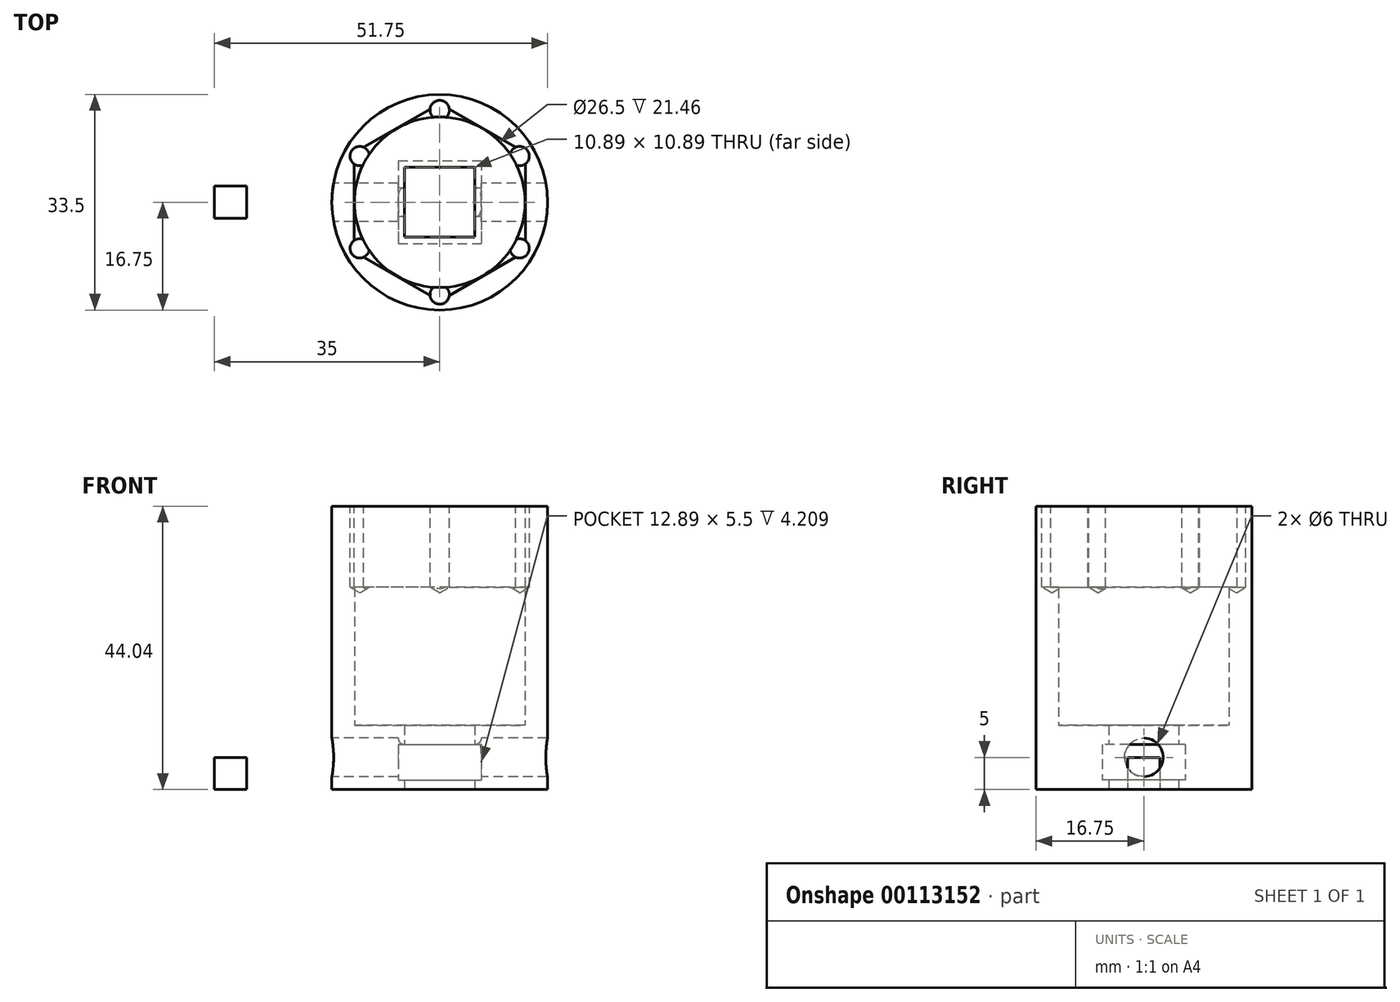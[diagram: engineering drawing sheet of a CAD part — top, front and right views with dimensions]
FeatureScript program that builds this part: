
annotation { "Feature Type Name" : "Feature", "Feature Type Description" : "" }
export const myFeature = defineFeature(function(context is Context, id is Id, definition is map)
    precondition{}
    {
        {
            var Q0;
            Q0=qCreatedBy(makeId("Top.planeOp"),FACE);
            var sketch = newSketch(context, id + "F0", { "sketchPlane" : qUnion([Q0])});
            skCircle(sketch, "E0", {"center": v(0, 0) * mm, "radius": 16.75 * mm});
            skLineSegment(sketch, "E1", {"start": v(0, 0) * mm, "end": v(0, 15.35) * mm});
            skLineSegment(sketch, "E2", {"start": v(0, 15.35) * mm, "end": v(-13.29, 7.67) * mm});
            skLineSegment(sketch, "E3", {"start": v(-13.3, 7.67) * mm, "end": v(-13.3, -7.67) * mm});
            skLineSegment(sketch, "E4", {"start": v(-13.3, -7.67) * mm, "end": v(0, -15.35) * mm});
            skLineSegment(sketch, "E5", {"start": v(0, -15.35) * mm, "end": v(13.29, -7.67) * mm});
            skLineSegment(sketch, "E6", {"start": v(13.29, -7.67) * mm, "end": v(13.29, 7.67) * mm});
            skLineSegment(sketch, "E7", {"start": v(0, 0) * mm, "end": v(0, -15.35) * mm});
            skLineSegment(sketch, "E8", {"start": v(0, 15.35) * mm, "end": v(13.3, 7.67) * mm});
            skLineSegment(sketch, "E9", {"start": v(0, 0) * mm, "end": v(13.29, 7.67) * mm});
            skLineSegment(sketch, "E10", {"start": v(0, 0) * mm, "end": v(13.29, -7.67) * mm});
            skLineSegment(sketch, "E11", {"start": v(0, 0) * mm, "end": v(-13.29, -7.67) * mm});
            skLineSegment(sketch, "E12", {"start": v(0, 0) * mm, "end": v(-13.3, 7.67) * mm});
            skCircle(sketch, "E13", {"center": v(0, 0) * mm, "radius": 15.75 * mm});
            skCircle(sketch, "E14", {"center": v(0, 0) * mm, "radius": 13.25 * mm});
            skLineSegment(sketch, "E15.bottom", {"start": v(-35, 2.5) * mm, "end": v(-30, 2.5) * mm});
            skLineSegment(sketch, "E15.top", {"start": v(-35, -2.5) * mm, "end": v(-30, -2.5) * mm});
            skLineSegment(sketch, "E15.left", {"start": v(-35, 2.5) * mm, "end": v(-35, -2.5) * mm});
            skLineSegment(sketch, "E15.right", {"start": v(-30, 2.5) * mm, "end": v(-30, -2.5) * mm});
            skPoint(sketch, "E15.middle", {"position": v(-32.5, 0) * mm});
            skLineSegment(sketch, "E16", {"start": v(-32.5, 0) * mm, "end": v(-35, 0) * mm});
            skLineSegment(sketch, "E17", {"start": v(-32.5, 0) * mm, "end": v(-30, 0) * mm});
            skLineSegment(sketch, "E18.bottom", {"start": v(-5.44, 5.45) * mm, "end": v(5.45, 5.45) * mm});
            skLineSegment(sketch, "E18.top", {"start": v(-5.45, -5.44) * mm, "end": v(5.44, -5.44) * mm});
            skLineSegment(sketch, "E18.left", {"start": v(-5.44, 5.45) * mm, "end": v(-5.45, -5.45) * mm});
            skLineSegment(sketch, "E18.right", {"start": v(5.45, 5.45) * mm, "end": v(5.44, -5.45) * mm});
            skLineSegment(sketch, "E19.bottom", {"start": v(-6.44, 6.45) * mm, "end": v(6.45, 6.45) * mm});
            skLineSegment(sketch, "E19.top", {"start": v(-6.45, -6.44) * mm, "end": v(6.44, -6.44) * mm});
            skLineSegment(sketch, "E19.left", {"start": v(-6.44, 6.45) * mm, "end": v(-6.45, -6.44) * mm});
            skLineSegment(sketch, "E19.right", {"start": v(6.45, 6.45) * mm, "end": v(6.44, -6.44) * mm});
            skSolve(sketch);
        }
        {
            var Q0;
            {var subQ0=sQuery(id+"F0.wireOp",EDGE,"E3");Q0=makeQuery(id+"F0.imprint","IMPRINT",FACE,{"disambiguationData":[TD([[makeQuery(id+"F0.imprint","IMPRINT",EDGE,{"derivedFrom":subQ0}),1.0]])]});}
            var Q1;
            {var subQ0=sQuery(id+"F0.wireOp",EDGE,"E4");Q1=makeQuery(id+"F0.imprint","IMPRINT",FACE,{"disambiguationData":[TD([[makeQuery(id+"F0.imprint","IMPRINT",EDGE,{"derivedFrom":subQ0}),1.0]])]});}
            var Q2;
            {var subQ0=sQuery(id+"F0.wireOp",EDGE,"E5");Q2=makeQuery(id+"F0.imprint","IMPRINT",FACE,{"disambiguationData":[TD([[makeQuery(id+"F0.imprint","IMPRINT",EDGE,{"derivedFrom":subQ0}),1.0]])]});}
            var Q3;
            {var subQ0=sQuery(id+"F0.wireOp",EDGE,"E8");Q3=makeQuery(id+"F0.imprint","IMPRINT",FACE,{"disambiguationData":[TD([[makeQuery(id+"F0.imprint","IMPRINT",EDGE,{"derivedFrom":subQ0}),-1.0]])]});}
            var Q4;
            {var subQ0=sQuery(id+"F0.wireOp",EDGE,"E2");Q4=makeQuery(id+"F0.imprint","IMPRINT",FACE,{"disambiguationData":[TD([[makeQuery(id+"F0.imprint","IMPRINT",EDGE,{"derivedFrom":subQ0}),1.0]])]});}
            var Q5;
            {var subQ0=sQuery(id+"F0.wireOp",EDGE,"E2");Q5=makeQuery(id+"F0.imprint","IMPRINT",FACE,{"disambiguationData":[TD([[makeQuery(id+"F0.imprint","IMPRINT",EDGE,{"derivedFrom":subQ0}),1.0]])]});}
            var Q6;
            {var subQ0=sQuery(id+"F0.wireOp",EDGE,"E6");Q6=makeQuery(id+"F0.imprint","IMPRINT",FACE,{"disambiguationData":[TD([[makeQuery(id+"F0.imprint","IMPRINT",EDGE,{"derivedFrom":subQ0}),1.0]])]});}
            extrude(context, id + "F1", {"entities" : qUnion([Q0, Q1, Q2, Q3, Q4, Q5, Q6]), "depth" : 31.46 * mm});
        }
        {
            var Q0;
            Q0=makeQuery(id+"F0.imprint","IMPRINT",FACE,{"disambiguationData":[TD([[makeQuery(id+"F0.imprint","IMPRINT",EDGE,{"derivedFrom":sQuery(id+"F0.wireOp",EDGE,"E0")}),1.0]])]});
            var Q1;
            Q1=makeQuery(id+"F0.imprint","IMPRINT",FACE,{"disambiguationData":[TD([[makeQuery(id+"F0.imprint","IMPRINT",EDGE,{"derivedFrom":sQuery(id+"F0.wireOp",EDGE,"E2")}),-1.0]])]});
            extrude(context, id + "F2", {"entities" : qUnion([Q0, Q1]), "operationType" : NewBodyOperationType.ADD, "depth" : 44.04 * mm});
        }
        {
            var Q0;
            {var subQ1=sQuery(id+"F0.wireOp",EDGE,"E11");var subQ3=sQuery(id+"F0.wireOp",EDGE,"E14");var subQ4=makeQuery(id+"F0.imprint","INTERSECT",VERTEX,{"derivedFrom":[subQ1,subQ3]});Q0=makeQuery(id+"F0.imprint","IMPRINT",FACE,{"disambiguationData":[TD([[makeQuery(id+"F0.imprint","IMPRINT",EDGE,{"disambiguationData":[TD([[subQ4,1.0]])],"derivedFrom":subQ3}),1.0]])]});}
            var Q1;
            {var subQ1=sQuery(id+"F0.wireOp",EDGE,"E1");var subQ3=sQuery(id+"F0.wireOp",EDGE,"E14");var subQ4=makeQuery(id+"F0.imprint","INTERSECT",VERTEX,{"derivedFrom":[subQ1,subQ3]});Q1=makeQuery(id+"F0.imprint","IMPRINT",FACE,{"disambiguationData":[TD([[makeQuery(id+"F0.imprint","IMPRINT",EDGE,{"disambiguationData":[TD([[subQ4,-1.0]])],"derivedFrom":subQ3}),1.0]])]});}
            var Q2;
            {var subQ1=sQuery(id+"F0.wireOp",EDGE,"E1");var subQ3=sQuery(id+"F0.wireOp",EDGE,"E14");var subQ4=makeQuery(id+"F0.imprint","INTERSECT",VERTEX,{"derivedFrom":[subQ1,subQ3]});Q2=makeQuery(id+"F0.imprint","IMPRINT",FACE,{"disambiguationData":[TD([[makeQuery(id+"F0.imprint","IMPRINT",EDGE,{"disambiguationData":[TD([[subQ4,1.0]])],"derivedFrom":subQ3}),1.0]])]});}
            var Q3;
            {var subQ1=sQuery(id+"F0.wireOp",EDGE,"E9");var subQ3=sQuery(id+"F0.wireOp",EDGE,"E14");var subQ4=makeQuery(id+"F0.imprint","INTERSECT",VERTEX,{"derivedFrom":[subQ1,subQ3]});Q3=makeQuery(id+"F0.imprint","IMPRINT",FACE,{"disambiguationData":[TD([[makeQuery(id+"F0.imprint","IMPRINT",EDGE,{"disambiguationData":[TD([[subQ4,1.0]])],"derivedFrom":subQ3}),1.0]])]});}
            var Q4;
            {var subQ1=sQuery(id+"F0.wireOp",EDGE,"E7");var subQ3=sQuery(id+"F0.wireOp",EDGE,"E14");var subQ4=makeQuery(id+"F0.imprint","INTERSECT",VERTEX,{"derivedFrom":[subQ1,subQ3]});Q4=makeQuery(id+"F0.imprint","IMPRINT",FACE,{"disambiguationData":[TD([[makeQuery(id+"F0.imprint","IMPRINT",EDGE,{"disambiguationData":[TD([[subQ4,-1.0]])],"derivedFrom":subQ3}),1.0]])]});}
            var Q5;
            {var subQ1=sQuery(id+"F0.wireOp",EDGE,"E7");var subQ3=sQuery(id+"F0.wireOp",EDGE,"E14");var subQ4=makeQuery(id+"F0.imprint","INTERSECT",VERTEX,{"derivedFrom":[subQ1,subQ3]});Q5=makeQuery(id+"F0.imprint","IMPRINT",FACE,{"disambiguationData":[TD([[makeQuery(id+"F0.imprint","IMPRINT",EDGE,{"disambiguationData":[TD([[subQ4,1.0]])],"derivedFrom":subQ3}),1.0]])]});}
            extrude(context, id + "F3", {"entities" : qUnion([Q0, Q1, Q2, Q3, Q4, Q5]), "operationType" : NewBodyOperationType.ADD, "depth" : 10 * mm});
        }
        {
            var Q0;
            Q0=makeQuery(id+"F2.opExtrude","CAP_FACE",FACE,{"disambiguationData":[OSD([sQuery(id+"F0.wireOp",EDGE,"E0"),sQuery(id+"F0.wireOp",EDGE,"E2"),sQuery(id+"F0.wireOp",EDGE,"E3"),sQuery(id+"F0.wireOp",EDGE,"E4"),sQuery(id+"F0.wireOp",EDGE,"E5"),sQuery(id+"F0.wireOp",EDGE,"E6"),sQuery(id+"F0.wireOp",EDGE,"E8")])],"isStart":false});
            var sketch = newSketch(context, id + "F4", { "sketchPlane" : qUnion([Q0])});
            skLineSegment(sketch, "E20", {"start": v(0, 15.35) * mm, "end": v(-13.29, 7.67) * mm});
            skLineSegment(sketch, "E21", {"start": v(-13.3, 7.67) * mm, "end": v(-13.29, -7.67) * mm});
            skLineSegment(sketch, "E22", {"start": v(-13.29, -7.67) * mm, "end": v(0, -15.35) * mm});
            skLineSegment(sketch, "E23", {"start": v(0, -15.35) * mm, "end": v(13.29, -7.67) * mm});
            skLineSegment(sketch, "E24", {"start": v(13.29, -7.67) * mm, "end": v(13.29, 7.67) * mm});
            skLineSegment(sketch, "E25", {"start": v(13.29, 7.67) * mm, "end": v(0, 15.35) * mm});
            skLineSegment(sketch, "E26", {"start": v(0, 15.35) * mm, "end": v(0, 14.35) * mm});
            skLineSegment(sketch, "E27", {"start": v(13.29, 7.67) * mm, "end": v(12.42, 7.17) * mm});
            skLineSegment(sketch, "E28", {"start": v(-13.29, 7.67) * mm, "end": v(-12.42, 7.17) * mm});
            skLineSegment(sketch, "E29", {"start": v(-13.3, -7.67) * mm, "end": v(-12.42, -7.17) * mm});
            skLineSegment(sketch, "E30", {"start": v(13.29, -7.67) * mm, "end": v(12.42, -7.17) * mm});
            skLineSegment(sketch, "E31", {"start": v(0, -15.35) * mm, "end": v(0, -14.35) * mm});
            skSolve(sketch);
        }
        {
            var Q0;
            Q0=sQuery(id+"F4.wireOp",VERTEX,"E28.end");
            var Q1;
            Q1=sQuery(id+"F4.wireOp",VERTEX,"E29.end");
            var Q2;
            Q2=sQuery(id+"F4.wireOp",VERTEX,"E31.end");
            var Q3;
            Q3=sQuery(id+"F4.wireOp",VERTEX,"E30.end");
            var Q4;
            Q4=sQuery(id+"F4.wireOp",VERTEX,"E27.end");
            var Q5;
            Q5=sQuery(id+"F4.wireOp",VERTEX,"E26.end");
            var Q6;
            Q6=makeQuery(id+"F1.opExtrude","SWEPT_BODY",BODY,{"disambiguationData":[OSD([sQuery(id+"F0.wireOp",EDGE,"E2"),sQuery(id+"F0.wireOp",EDGE,"E3"),sQuery(id+"F0.wireOp",EDGE,"E4"),sQuery(id+"F0.wireOp",EDGE,"E5"),sQuery(id+"F0.wireOp",EDGE,"E6"),sQuery(id+"F0.wireOp",EDGE,"E8"),sQuery(id+"F0.wireOp",EDGE,"E14")])]});
            hole(context, id + "F5", {"style" : HoleStyle.SIMPLE, "endStyle" : HoleEndStyle.BLIND, "holeDiameter" : 3 * mm, "holeDepth" : 12.58 * mm, "startFromSketch" : true, "locations" : qUnion([Q0, Q1, Q2, Q3, Q4, Q5]), "scope" : qUnion([Q6])});
        }
        {
            var Q0;
            {var subQ2=sQuery(id+"F0.wireOp",EDGE,"E15.bottom");Q0=makeQuery(id+"F0.imprint","IMPRINT",FACE,{"disambiguationData":[TD([[makeQuery(id+"F0.imprint","IMPRINT",EDGE,{"derivedFrom":subQ2}),-1.0]])]});}
            var Q1;
            {var subQ2=sQuery(id+"F0.wireOp",EDGE,"E15.top");Q1=makeQuery(id+"F0.imprint","IMPRINT",FACE,{"disambiguationData":[TD([[makeQuery(id+"F0.imprint","IMPRINT",EDGE,{"derivedFrom":subQ2}),1.0]])]});}
            extrude(context, id + "F6", {"entities" : qUnion([Q0, Q1]), "depth" : 5 * mm});
        }
        {
            var Q0;
            Q0=makeQuery(id+"F6.opExtrude","SWEPT_FACE",FACE,{"disambiguationData":[OSD([sQuery(id+"F0.wireOp",EDGE,"E15.left")])]});
            var sketch = newSketch(context, id + "F7", { "sketchPlane" : qUnion([Q0])});
            skLineSegment(sketch, "E32", {"start": v(-2.5, 5) * mm, "end": v(0, 5) * mm});
            skSolve(sketch);
        }
        {
            var Q0;
            Q0=sQuery(id+"F7.wireOp",VERTEX,"E32.end");
            var Q1;
            Q1=makeQuery(id+"F1.opExtrude","SWEPT_BODY",BODY,{"disambiguationData":[OSD([sQuery(id+"F0.wireOp",EDGE,"E2"),sQuery(id+"F0.wireOp",EDGE,"E3"),sQuery(id+"F0.wireOp",EDGE,"E4"),sQuery(id+"F0.wireOp",EDGE,"E5"),sQuery(id+"F0.wireOp",EDGE,"E6"),sQuery(id+"F0.wireOp",EDGE,"E8"),sQuery(id+"F0.wireOp",EDGE,"E14")])]});
            hole(context, id + "F8", {"style" : HoleStyle.SIMPLE, "endStyle" : HoleEndStyle.THROUGH, "holeDiameter" : 6 * mm, "startFromSketch" : true, "locations" : qUnion([Q0]), "scope" : qUnion([Q1]), "isTappedThrough" : true});
        }
        {
            var Q0;
            {var subQ1=sQuery(id+"F0.wireOp",EDGE,"E18.bottom");var subQ5=sQuery(id+"F0.wireOp",EDGE,"E1");var subQ6=makeQuery(id+"F0.imprint","INTERSECT",VERTEX,{"derivedFrom":[subQ5,subQ1]});Q0=makeQuery(id+"F0.imprint","IMPRINT",FACE,{"disambiguationData":[TD([[makeQuery(id+"F0.imprint","IMPRINT",EDGE,{"disambiguationData":[TD([[subQ6,-1.0]])],"derivedFrom":subQ5}),1.0]])]});}
            var Q1;
            {var subQ1=sQuery(id+"F0.wireOp",EDGE,"E18.bottom");var subQ3=sQuery(id+"F0.wireOp",EDGE,"E1");var subQ4=makeQuery(id+"F0.imprint","INTERSECT",VERTEX,{"derivedFrom":[subQ3,subQ1]});Q1=makeQuery(id+"F0.imprint","IMPRINT",FACE,{"disambiguationData":[TD([[makeQuery(id+"F0.imprint","IMPRINT",EDGE,{"disambiguationData":[TD([[subQ4,-1.0]])],"derivedFrom":subQ3}),-1.0]])]});}
            var Q2;
            {var subQ0=sQuery(id+"F0.wireOp",EDGE,"E18.right");var subQ1=sQuery(id+"F0.wireOp",EDGE,"E9");var subQ2=makeQuery(id+"F0.imprint","INTERSECT",VERTEX,{"derivedFrom":[subQ1,subQ0]});Q2=makeQuery(id+"F0.imprint","IMPRINT",FACE,{"disambiguationData":[TD([[makeQuery(id+"F0.imprint","IMPRINT",EDGE,{"disambiguationData":[TD([[subQ2,-1.0]])],"derivedFrom":subQ1}),-1.0]])]});}
            var Q3;
            {var subQ1=sQuery(id+"F0.wireOp",EDGE,"E18.top");var subQ5=sQuery(id+"F0.wireOp",EDGE,"E7");var subQ6=makeQuery(id+"F0.imprint","INTERSECT",VERTEX,{"derivedFrom":[subQ5,subQ1]});Q3=makeQuery(id+"F0.imprint","IMPRINT",FACE,{"disambiguationData":[TD([[makeQuery(id+"F0.imprint","IMPRINT",EDGE,{"disambiguationData":[TD([[subQ6,-1.0]])],"derivedFrom":subQ5}),1.0]])]});}
            var Q4;
            {var subQ1=sQuery(id+"F0.wireOp",EDGE,"E18.top");var subQ5=sQuery(id+"F0.wireOp",EDGE,"E7");var subQ6=makeQuery(id+"F0.imprint","INTERSECT",VERTEX,{"derivedFrom":[subQ5,subQ1]});Q4=makeQuery(id+"F0.imprint","IMPRINT",FACE,{"disambiguationData":[TD([[makeQuery(id+"F0.imprint","IMPRINT",EDGE,{"disambiguationData":[TD([[subQ6,-1.0]])],"derivedFrom":subQ5}),-1.0]])]});}
            var Q5;
            {var subQ0=sQuery(id+"F0.wireOp",EDGE,"E18.left");var subQ1=sQuery(id+"F0.wireOp",EDGE,"E11");var subQ2=makeQuery(id+"F0.imprint","INTERSECT",VERTEX,{"derivedFrom":[subQ1,subQ0]});Q5=makeQuery(id+"F0.imprint","IMPRINT",FACE,{"disambiguationData":[TD([[makeQuery(id+"F0.imprint","IMPRINT",EDGE,{"disambiguationData":[TD([[subQ2,-1.0]])],"derivedFrom":subQ1}),-1.0]])]});}
            extrude(context, id + "F9", {"entities" : qUnion([Q0, Q1, Q2, Q3, Q4, Q5]), "operationType" : NewBodyOperationType.ADD, "depth" : 10 * mm, "hasSecondDirection" : true, "secondDirectionOppositeDirection" : false, "secondDirectionDepth" : 7 * mm});
        }
        {
            var Q0;
            {var subQ1=sQuery(id+"F0.wireOp",EDGE,"E18.bottom");var subQ5=sQuery(id+"F0.wireOp",EDGE,"E1");var subQ6=makeQuery(id+"F0.imprint","INTERSECT",VERTEX,{"derivedFrom":[subQ5,subQ1]});Q0=makeQuery(id+"F0.imprint","IMPRINT",FACE,{"disambiguationData":[TD([[makeQuery(id+"F0.imprint","IMPRINT",EDGE,{"disambiguationData":[TD([[subQ6,-1.0]])],"derivedFrom":subQ5}),1.0]])]});}
            var Q1;
            {var subQ1=sQuery(id+"F0.wireOp",EDGE,"E18.bottom");var subQ3=sQuery(id+"F0.wireOp",EDGE,"E1");var subQ4=makeQuery(id+"F0.imprint","INTERSECT",VERTEX,{"derivedFrom":[subQ3,subQ1]});Q1=makeQuery(id+"F0.imprint","IMPRINT",FACE,{"disambiguationData":[TD([[makeQuery(id+"F0.imprint","IMPRINT",EDGE,{"disambiguationData":[TD([[subQ4,-1.0]])],"derivedFrom":subQ3}),-1.0]])]});}
            var Q2;
            {var subQ0=sQuery(id+"F0.wireOp",EDGE,"E18.right");var subQ1=sQuery(id+"F0.wireOp",EDGE,"E9");var subQ2=makeQuery(id+"F0.imprint","INTERSECT",VERTEX,{"derivedFrom":[subQ1,subQ0]});Q2=makeQuery(id+"F0.imprint","IMPRINT",FACE,{"disambiguationData":[TD([[makeQuery(id+"F0.imprint","IMPRINT",EDGE,{"disambiguationData":[TD([[subQ2,-1.0]])],"derivedFrom":subQ1}),-1.0]])]});}
            var Q3;
            {var subQ1=sQuery(id+"F0.wireOp",EDGE,"E18.top");var subQ5=sQuery(id+"F0.wireOp",EDGE,"E7");var subQ6=makeQuery(id+"F0.imprint","INTERSECT",VERTEX,{"derivedFrom":[subQ5,subQ1]});Q3=makeQuery(id+"F0.imprint","IMPRINT",FACE,{"disambiguationData":[TD([[makeQuery(id+"F0.imprint","IMPRINT",EDGE,{"disambiguationData":[TD([[subQ6,-1.0]])],"derivedFrom":subQ5}),1.0]])]});}
            var Q4;
            {var subQ1=sQuery(id+"F0.wireOp",EDGE,"E18.top");var subQ5=sQuery(id+"F0.wireOp",EDGE,"E7");var subQ6=makeQuery(id+"F0.imprint","INTERSECT",VERTEX,{"derivedFrom":[subQ5,subQ1]});Q4=makeQuery(id+"F0.imprint","IMPRINT",FACE,{"disambiguationData":[TD([[makeQuery(id+"F0.imprint","IMPRINT",EDGE,{"disambiguationData":[TD([[subQ6,-1.0]])],"derivedFrom":subQ5}),-1.0]])]});}
            var Q5;
            {var subQ0=sQuery(id+"F0.wireOp",EDGE,"E18.left");var subQ1=sQuery(id+"F0.wireOp",EDGE,"E11");var subQ2=makeQuery(id+"F0.imprint","INTERSECT",VERTEX,{"derivedFrom":[subQ1,subQ0]});Q5=makeQuery(id+"F0.imprint","IMPRINT",FACE,{"disambiguationData":[TD([[makeQuery(id+"F0.imprint","IMPRINT",EDGE,{"disambiguationData":[TD([[subQ2,-1.0]])],"derivedFrom":subQ1}),-1.0]])]});}
            extrude(context, id + "F10", {"entities" : qUnion([Q0, Q1, Q2, Q3, Q4, Q5]), "operationType" : NewBodyOperationType.ADD, "depth" : 1.5 * mm});
        }
        {
            var Q0;
            Q0=makeQuery(id+"F9.opExtrude","CAP_EDGE",EDGE,{"disambiguationData":[OSD([sQuery(id+"F0.wireOp",EDGE,"E19.bottom")])],"isStart":true});
            var Q1;
            {var subQ0=sQuery(id+"F0.wireOp",EDGE,"E19.left");var subQ1=sQuery(id+"F0.wireOp",EDGE,"E19.bottom");Q1=makeQuery(id+"F9.boolean.opBoolean","SPLIT",EDGE,{"disambiguationData":[TD([makeQuery(id+"F3.opExtrude","SWEPT_FACE",FACE,{"disambiguationData":[OSD([subQ1])]}),makeQuery(id+"F3.opExtrude","SWEPT_FACE",FACE,{"disambiguationData":[OSD([subQ0])]}),makeQuery(id+"F8.hole-0.boolean.opBoolean","COPY",FACE,{"disambiguationData":[OD(0.0)],"derivedFrom":makeQuery(id+"F8.hole-0.opRevolve","SWEPT_FACE",FACE,{"disambiguationData":[OSD([sQuery(id+"F8.hole-0.sketch.wireOp",EDGE,"core_line_2")])]})}),makeQuery(id+"F9.opExtrude","CAP_FACE",FACE,{"disambiguationData":[OSD([sQuery(id+"F0.wireOp",EDGE,"E18.bottom"),sQuery(id+"F0.wireOp",EDGE,"E18.top"),sQuery(id+"F0.wireOp",EDGE,"E18.left"),sQuery(id+"F0.wireOp",EDGE,"E18.right"),subQ1,sQuery(id+"F0.wireOp",EDGE,"E19.top"),subQ0,sQuery(id+"F0.wireOp",EDGE,"E19.right")])],"isStart":true}),makeQuery(id+"F9.opExtrude","SWEPT_FACE",FACE,{"disambiguationData":[OSD([subQ0])]})])],"derivedFrom":makeQuery(id+"F9.opExtrude","CAP_EDGE",EDGE,{"disambiguationData":[OSD([subQ0])],"isStart":true})});}
            var Q2;
            {var subQ0=sQuery(id+"F0.wireOp",EDGE,"E19.right");var subQ1=sQuery(id+"F0.wireOp",EDGE,"E19.top");Q2=makeQuery(id+"F9.boolean.opBoolean","SPLIT",EDGE,{"disambiguationData":[TD([makeQuery(id+"F3.opExtrude","SWEPT_FACE",FACE,{"disambiguationData":[OSD([subQ1])]}),makeQuery(id+"F3.opExtrude","SWEPT_FACE",FACE,{"disambiguationData":[OSD([subQ0])]}),makeQuery(id+"F8.hole-0.boolean.opBoolean","COPY",FACE,{"disambiguationData":[OD(1.0)],"derivedFrom":makeQuery(id+"F8.hole-0.opRevolve","SWEPT_FACE",FACE,{"disambiguationData":[OSD([sQuery(id+"F8.hole-0.sketch.wireOp",EDGE,"core_line_2")])]})}),makeQuery(id+"F9.opExtrude","CAP_FACE",FACE,{"disambiguationData":[OSD([sQuery(id+"F0.wireOp",EDGE,"E18.bottom"),sQuery(id+"F0.wireOp",EDGE,"E18.top"),sQuery(id+"F0.wireOp",EDGE,"E18.left"),sQuery(id+"F0.wireOp",EDGE,"E18.right"),sQuery(id+"F0.wireOp",EDGE,"E19.bottom"),subQ1,sQuery(id+"F0.wireOp",EDGE,"E19.left"),subQ0])],"isStart":true}),makeQuery(id+"F9.opExtrude","SWEPT_FACE",FACE,{"disambiguationData":[OSD([subQ0])]})])],"derivedFrom":makeQuery(id+"F9.opExtrude","CAP_EDGE",EDGE,{"disambiguationData":[OSD([subQ0])],"isStart":true})});}
            var Q3;
            {var subQ0=sQuery(id+"F0.wireOp",EDGE,"E19.right");var subQ1=sQuery(id+"F0.wireOp",EDGE,"E19.bottom");Q3=makeQuery(id+"F9.boolean.opBoolean","SPLIT",EDGE,{"disambiguationData":[TD([makeQuery(id+"F3.opExtrude","SWEPT_FACE",FACE,{"disambiguationData":[OSD([subQ1])]}),makeQuery(id+"F3.opExtrude","SWEPT_FACE",FACE,{"disambiguationData":[OSD([subQ0])]}),makeQuery(id+"F8.hole-0.boolean.opBoolean","COPY",FACE,{"disambiguationData":[OD(1.0)],"derivedFrom":makeQuery(id+"F8.hole-0.opRevolve","SWEPT_FACE",FACE,{"disambiguationData":[OSD([sQuery(id+"F8.hole-0.sketch.wireOp",EDGE,"core_line_2")])]})}),makeQuery(id+"F9.opExtrude","CAP_FACE",FACE,{"disambiguationData":[OSD([sQuery(id+"F0.wireOp",EDGE,"E18.bottom"),sQuery(id+"F0.wireOp",EDGE,"E18.top"),sQuery(id+"F0.wireOp",EDGE,"E18.left"),sQuery(id+"F0.wireOp",EDGE,"E18.right"),subQ1,sQuery(id+"F0.wireOp",EDGE,"E19.top"),sQuery(id+"F0.wireOp",EDGE,"E19.left"),subQ0])],"isStart":true}),makeQuery(id+"F9.opExtrude","SWEPT_FACE",FACE,{"disambiguationData":[OSD([subQ0])]})])],"derivedFrom":makeQuery(id+"F9.opExtrude","CAP_EDGE",EDGE,{"disambiguationData":[OSD([subQ0])],"isStart":true})});}
            var Q4;
            Q4=makeQuery(id+"F9.opExtrude","CAP_EDGE",EDGE,{"disambiguationData":[OSD([sQuery(id+"F0.wireOp",EDGE,"E19.top")])],"isStart":true});
            var Q5;
            {var subQ0=sQuery(id+"F0.wireOp",EDGE,"E19.left");var subQ1=sQuery(id+"F0.wireOp",EDGE,"E19.top");Q5=makeQuery(id+"F9.boolean.opBoolean","SPLIT",EDGE,{"disambiguationData":[TD([makeQuery(id+"F3.opExtrude","SWEPT_FACE",FACE,{"disambiguationData":[OSD([subQ1])]}),makeQuery(id+"F3.opExtrude","SWEPT_FACE",FACE,{"disambiguationData":[OSD([subQ0])]}),makeQuery(id+"F8.hole-0.boolean.opBoolean","COPY",FACE,{"disambiguationData":[OD(0.0)],"derivedFrom":makeQuery(id+"F8.hole-0.opRevolve","SWEPT_FACE",FACE,{"disambiguationData":[OSD([sQuery(id+"F8.hole-0.sketch.wireOp",EDGE,"core_line_2")])]})}),makeQuery(id+"F9.opExtrude","CAP_FACE",FACE,{"disambiguationData":[OSD([sQuery(id+"F0.wireOp",EDGE,"E18.bottom"),sQuery(id+"F0.wireOp",EDGE,"E18.top"),sQuery(id+"F0.wireOp",EDGE,"E18.left"),sQuery(id+"F0.wireOp",EDGE,"E18.right"),sQuery(id+"F0.wireOp",EDGE,"E19.bottom"),subQ1,subQ0,sQuery(id+"F0.wireOp",EDGE,"E19.right")])],"isStart":true}),makeQuery(id+"F9.opExtrude","SWEPT_FACE",FACE,{"disambiguationData":[OSD([subQ0])]})])],"derivedFrom":makeQuery(id+"F9.opExtrude","CAP_EDGE",EDGE,{"disambiguationData":[OSD([subQ0])],"isStart":true})});}
            var Q6;
            Q6=makeQuery(id+"F10.opExtrude","CAP_EDGE",EDGE,{"disambiguationData":[OSD([sQuery(id+"F0.wireOp",EDGE,"E19.left")])],"isStart":false});
            var Q7;
            Q7=makeQuery(id+"F10.opExtrude","CAP_EDGE",EDGE,{"disambiguationData":[OSD([sQuery(id+"F0.wireOp",EDGE,"E19.bottom")])],"isStart":false});
            var Q8;
            Q8=makeQuery(id+"F10.opExtrude","CAP_EDGE",EDGE,{"disambiguationData":[OSD([sQuery(id+"F0.wireOp",EDGE,"E19.right")])],"isStart":false});
            var Q9;
            Q9=makeQuery(id+"F10.opExtrude","CAP_EDGE",EDGE,{"disambiguationData":[OSD([sQuery(id+"F0.wireOp",EDGE,"E19.top")])],"isStart":false});
            fillet(context, id + "F11", {"entities" : qUnion([Q0, Q1, Q2, Q3, Q4, Q5, Q6, Q7, Q8, Q9]), "radius" : 1 * mm, "tangentPropagation" : true, "allowEdgeOverflow" : false});
        }
    });
